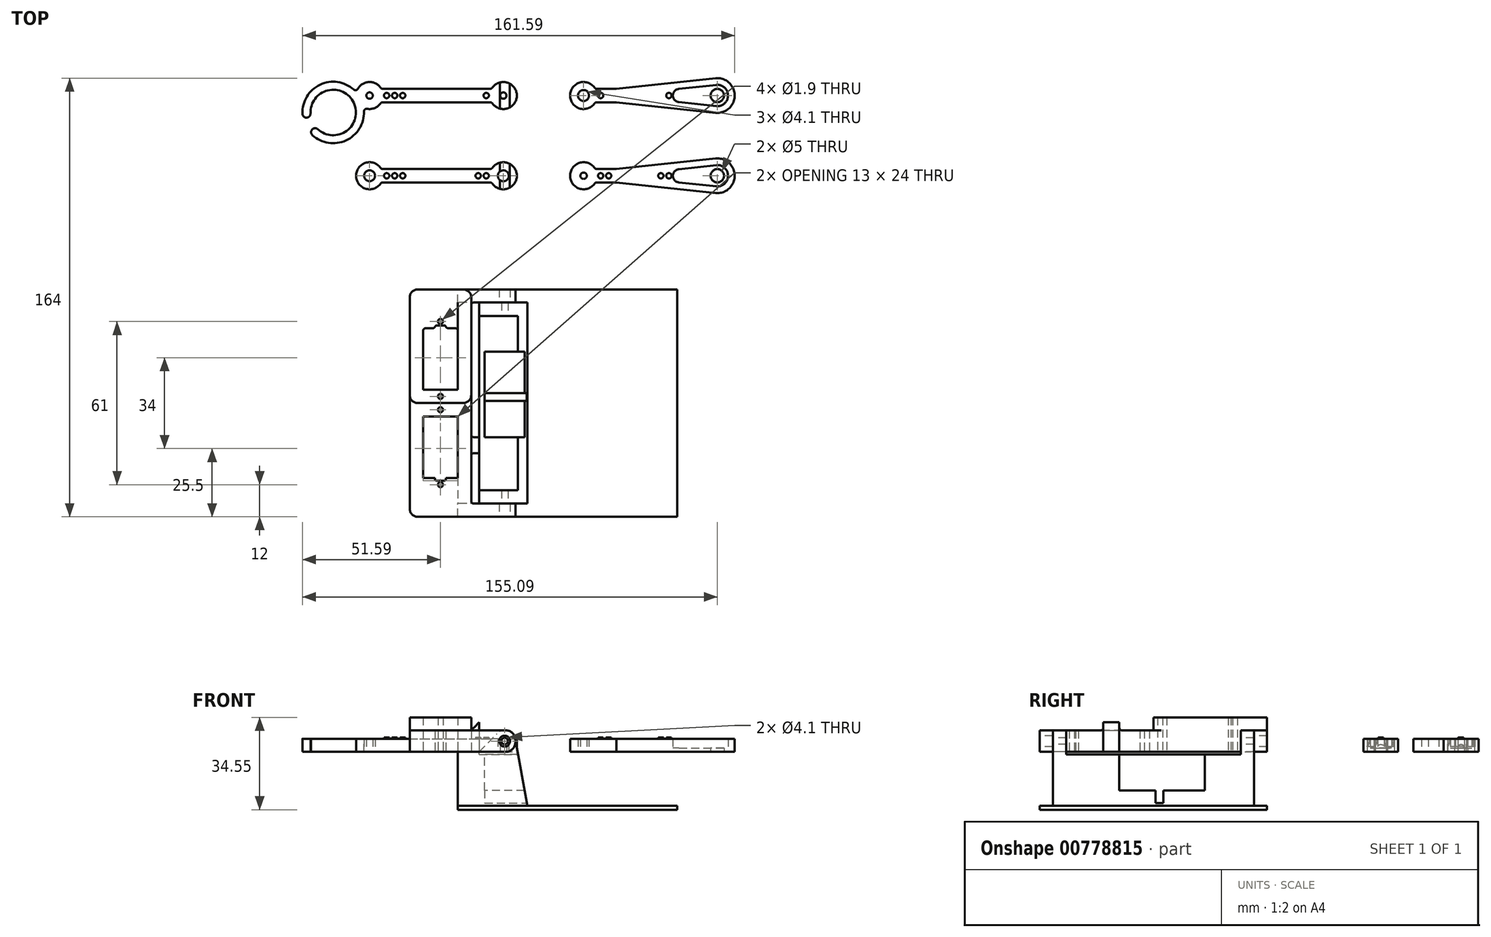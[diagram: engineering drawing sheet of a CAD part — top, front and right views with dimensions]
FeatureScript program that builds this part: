
annotation { "Feature Type Name" : "Feature", "Feature Type Description" : "" }
export const myFeature = defineFeature(function(context is Context, id is Id, definition is map)
    precondition{}
    {
        {
            assignVariable(context, id + "F0", {"name" : "armThickness", "anyValue" : 4.9 * mm});
        }
        {
            assignVariable(context, id + "F1", {"name" : "servoMountThick", "anyValue" : 1.5 * mm});
        }
        {
            var Q0;
            Q0=qCreatedBy(makeId("Top.planeOp"),FACE);
            var sketch = newSketch(context, id + "F2", { "sketchPlane" : qUnion([Q0])});
            skLineSegment(sketch, "E0", {"start": v(-65, 85) * mm, "end": v(-15, 85) * mm, "construction": true});
            skArc(sketch, "E1", {"start": v(-60.61, 87.5) * mm, "mid": v(-70.05, 85) * mm, "end": v(-60.61, 82.5) * mm});
            skArc(sketch, "E2", {"start": v(-19.39, 82.5) * mm, "mid": v(-9.95, 85) * mm, "end": v(-19.39, 87.5) * mm});
            skCircle(sketch, "E3", {"center": v(-65, 85) * mm, "radius": 2.05 * mm});
            skCircle(sketch, "E4", {"center": v(-15, 85) * mm, "radius": 2.05 * mm});
            skLineSegment(sketch, "E5", {"start": v(-60.61, 87.5) * mm, "end": v(-19.39, 87.5) * mm});
            skLineSegment(sketch, "E6", {"start": v(-60.61, 82.5) * mm, "end": v(-19.39, 82.5) * mm});
            skLineSegment(sketch, "E7", {"start": v(-40, 85) * mm, "end": v(-40, 87.5) * mm, "construction": true});
            skLineSegment(sketch, "E8", {"start": v(-40, 85) * mm, "end": v(-40, 82.5) * mm, "construction": true});
            skLineSegment(sketch, "E9", {"start": v(-65, 115) * mm, "end": v(-15, 115) * mm, "construction": true});
            skCircle(sketch, "E10", {"center": v(-15, 115) * mm, "radius": 1.2 * mm});
            skCircle(sketch, "E11", {"center": v(-65, 115) * mm, "radius": 1.2 * mm});
            skArc(sketch, "E12", {"start": v(-60.61, 117.5) * mm, "mid": v(-65.7, 120) * mm, "end": v(-69.9, 116.2) * mm});
            skArc(sketch, "E13", {"start": v(-19.39, 112.5) * mm, "mid": v(-9.95, 115) * mm, "end": v(-19.39, 117.5) * mm});
            skLineSegment(sketch, "E14", {"start": v(-60.61, 117.5) * mm, "end": v(-19.39, 117.5) * mm});
            skLineSegment(sketch, "E15", {"start": v(-19.39, 112.5) * mm, "end": v(-60.61, 112.5) * mm});
            skLineSegment(sketch, "E16", {"start": v(-40, 115) * mm, "end": v(-40, 117.5) * mm, "construction": true});
            skLineSegment(sketch, "E17", {"start": v(-40, 115) * mm, "end": v(-40, 112.5) * mm, "construction": true});
            skArc(sketch, "E18", {"start": v(-69.9, 116.2) * mm, "mid": v(-82.85, 119.34) * mm, "end": v(-90.08, 108.16) * mm});
            skArc(sketch, "E19", {"start": v(-84.34, 102.4) * mm, "mid": v(-70.9, 112.25) * mm, "end": v(-87.09, 108.29) * mm});
            skLineSegment(sketch, "E20", {"start": v(-78.6, 108.66) * mm, "end": v(-65, 115) * mm, "construction": true});
            skLineSegment(sketch, "E21", {"start": v(-78.6, 108.66) * mm, "end": v(-86.36, 100.18) * mm, "construction": true});
            skLineSegment(sketch, "E22", {"start": v(-78.6, 108.66) * mm, "end": v(-90.08, 108.16) * mm, "construction": true});
            skLineSegment(sketch, "E23", {"start": v(-90.08, 108.16) * mm, "end": v(-86.36, 100.18) * mm, "construction": true});
            skLineSegment(sketch, "E24", {"start": v(-88.22, 104.17) * mm, "end": v(-78.6, 108.66) * mm, "construction": true});
            skArc(sketch, "E25.trimOffspring", {"start": v(-67.24, 110.47) * mm, "mid": v(-63.52, 110.17) * mm, "end": v(-60.61, 112.5) * mm});
            skArc(sketch, "E26", {"start": v(-90.08, 108.16) * mm, "mid": v(-88.52, 106.73) * mm, "end": v(-87.09, 108.29) * mm});
            skArc(sketch, "E27", {"start": v(-84.34, 102.4) * mm, "mid": v(-86.46, 102.3) * mm, "end": v(-86.36, 100.18) * mm});
            skArc(sketch, "E28.trimOffspring", {"start": v(-86.36, 100.18) * mm, "mid": v(-73.15, 98.53) * mm, "end": v(-67.24, 110.47) * mm});
            skCircle(sketch, "E29", {"center": v(15, 115) * mm, "radius": 2.05 * mm});
            skArc(sketch, "E30", {"start": v(19.39, 117.5) * mm, "mid": v(9.95, 115) * mm, "end": v(19.39, 112.5) * mm});
            skArc(sketch, "E31", {"start": v(64.3, 108.54) * mm, "mid": v(71.5, 115) * mm, "end": v(64.3, 121.46) * mm});
            skLineSegment(sketch, "E32", {"start": v(65, 115) * mm, "end": v(15, 115) * mm, "construction": true});
            skLineSegment(sketch, "E33.bottom", {"start": v(15, 85) * mm, "end": v(-15, 85) * mm, "construction": true});
            skLineSegment(sketch, "E33.top", {"start": v(15, 115) * mm, "end": v(-15, 115) * mm, "construction": true});
            skLineSegment(sketch, "E33.left", {"start": v(15, 85) * mm, "end": v(15, 115) * mm, "construction": true});
            skLineSegment(sketch, "E33.right", {"start": v(-15, 85) * mm, "end": v(-15, 115) * mm, "construction": true});
            skPoint(sketch, "E33.middle", {"position": v(0, 100) * mm});
            skArc(sketch, "E34", {"start": v(64.63, 111.52) * mm, "mid": v(68.5, 115) * mm, "end": v(64.63, 118.48) * mm, "construction": true});
            skArc(sketch, "E35", {"start": v(50.69, 116.99) * mm, "mid": v(48.9, 115) * mm, "end": v(50.69, 113.01) * mm, "construction": true});
            skLineSegment(sketch, "E36", {"start": v(50.69, 116.99) * mm, "end": v(64.63, 118.48) * mm, "construction": true});
            skLineSegment(sketch, "E37", {"start": v(64.63, 111.52) * mm, "end": v(50.69, 113.01) * mm, "construction": true});
            skCircle(sketch, "E38", {"center": v(65, 115) * mm, "radius": 2.5 * mm});
            skLineSegment(sketch, "E39", {"start": v(-15, 100) * mm, "end": v(15, 100) * mm, "construction": true});
            skArc(sketch, "E40.MirrorCS", {"start": v(64.63, 88.48) * mm, "mid": v(68.5, 85) * mm, "end": v(64.63, 81.52) * mm, "construction": true});
            skArc(sketch, "E41.MirrorCS", {"start": v(50.69, 83.01) * mm, "mid": v(48.9, 85) * mm, "end": v(50.69, 86.99) * mm, "construction": true});
            skLineSegment(sketch, "E42.MirrorCS", {"start": v(50.69, 83.01) * mm, "end": v(64.63, 81.52) * mm, "construction": true});
            skCircle(sketch, "E43.MirrorC", {"center": v(65, 85) * mm, "radius": 2.5 * mm});
            skCircle(sketch, "E44.MirrorC", {"center": v(15, 85) * mm, "radius": 1.2 * mm});
            skLineSegment(sketch, "E45.MirrorCS", {"start": v(64.63, 88.48) * mm, "end": v(50.69, 86.99) * mm, "construction": true});
            skLineSegment(sketch, "E46.MirrorCS", {"start": v(65, 85) * mm, "end": v(15, 85) * mm, "construction": true});
            skArc(sketch, "E47.MirrorCS", {"start": v(19.39, 82.5) * mm, "mid": v(9.95, 85) * mm, "end": v(19.39, 87.5) * mm});
            skArc(sketch, "E48.MirrorCS", {"start": v(64.3, 91.46) * mm, "mid": v(71.5, 85) * mm, "end": v(64.3, 78.54) * mm});
            skLineSegment(sketch, "E49", {"start": v(64.3, 121.46) * mm, "end": v(27.27, 117.5) * mm});
            skLineSegment(sketch, "E50", {"start": v(27.27, 117.5) * mm, "end": v(19.39, 117.5) * mm});
            skLineSegment(sketch, "E51", {"start": v(19.39, 117.5) * mm, "end": v(19.39, 115) * mm, "construction": true});
            skLineSegment(sketch, "E52.MirrorCS", {"start": v(64.3, 108.54) * mm, "end": v(27.27, 112.5) * mm});
            skLineSegment(sketch, "E53.MirrorCS", {"start": v(27.27, 112.5) * mm, "end": v(19.39, 112.5) * mm});
            skLineSegment(sketch, "E54.MirrorCS", {"start": v(64.3, 91.46) * mm, "end": v(27.27, 87.5) * mm});
            skLineSegment(sketch, "E55.MirrorCS", {"start": v(27.27, 87.5) * mm, "end": v(19.39, 87.5) * mm});
            skLineSegment(sketch, "E56.MirrorCS", {"start": v(64.3, 78.54) * mm, "end": v(27.27, 82.5) * mm});
            skLineSegment(sketch, "E57.MirrorCS", {"start": v(27.27, 82.5) * mm, "end": v(19.39, 82.5) * mm});
            skCircle(sketch, "E58", {"center": v(-58.61, 115) * mm, "radius": 1 * mm, "construction": true});
            skCircle(sketch, "E59", {"center": v(-55.61, 115) * mm, "radius": 1 * mm, "construction": true});
            skCircle(sketch, "E60", {"center": v(-52.61, 115) * mm, "radius": 1 * mm, "construction": true});
            skCircle(sketch, "E61.MirrorC", {"center": v(-52.61, 85) * mm, "radius": 1 * mm, "construction": true});
            skCircle(sketch, "E62.MirrorC", {"center": v(-55.61, 85) * mm, "radius": 1 * mm, "construction": true});
            skCircle(sketch, "E63.MirrorC", {"center": v(-58.61, 85) * mm, "radius": 1 * mm, "construction": true});
            skCircle(sketch, "E64.MirrorC", {"center": v(-21.39, 115) * mm, "radius": 1 * mm, "construction": true});
            skCircle(sketch, "E65.MirrorC", {"center": v(-24.39, 85) * mm, "radius": 1 * mm, "construction": true});
            skCircle(sketch, "E66.MirrorC", {"center": v(-21.39, 85) * mm, "radius": 1 * mm, "construction": true});
            skLineSegment(sketch, "E67", {"start": v(0, 100) * mm, "end": v(0, 115) * mm, "construction": true});
            skCircle(sketch, "E68.MirrorC", {"center": v(21.39, 115) * mm, "radius": 1 * mm, "construction": true});
            skCircle(sketch, "E69.MirrorC", {"center": v(21.39, 85) * mm, "radius": 1 * mm, "construction": true});
            skCircle(sketch, "E70.MirrorC", {"center": v(24.39, 85) * mm, "radius": 1 * mm, "construction": true});
            skCircle(sketch, "E71", {"center": v(46.9, 115) * mm, "radius": 1 * mm, "construction": true});
            skCircle(sketch, "E72.MirrorC", {"center": v(46.9, 85) * mm, "radius": 1 * mm, "construction": true});
            skCircle(sketch, "E73", {"center": v(43.9, 85) * mm, "radius": 1 * mm, "construction": true});
            skSolve(sketch);
        }
        {
            var Q0;
            Q0 = qSketchRegion(id + "F2", true);
            extrude(context, id + "F3", {"entities" : qUnion([Q0]), "depth" : getVariable(context, 'armThickness'), "offsetDistance" : 25 * mm});
        }
        {
            var Q0;
            Q0=makeQuery(id+"F3.opExtrude","CAP_FACE",FACE,{"disambiguationData":[OSD([sQuery(id+"F2.wireOp",EDGE,"E29"),sQuery(id+"F2.wireOp",EDGE,"E30"),sQuery(id+"F2.wireOp",EDGE,"n4DpriQ1-nnHI-GnaH-HkeK-Vg4Ocvjjlzz4"),sQuery(id+"F2.wireOp",EDGE,"E31"),sQuery(id+"F2.wireOp",EDGE,"Jy9hjOYC-l6QO-X5wc-15VK-UPtCCQa5w7qG"),sQuery(id+"F2.wireOp",EDGE,"E7qWX5Tq-FMOK-UQwe-IjNl-v5n85ifmwsZO")])],"isStart":false});
            cPlane(context, id + "F4", {"entities" : qUnion([Q0]), "cplaneType" : CPlaneType.OFFSET, "offset" : 3.5 * mm, "oppositeDirection" : true, "width" : 150 * mm, "height" : 150 * mm});
        }
        {
            var Q0;
            Q0=qCreatedBy(id+"F4.planeOp",FACE);
            var sketch = newSketch(context, id + "F5", { "sketchPlane" : qUnion([Q0])});
            skLineSegment(sketch, "E74.0", {"start": v(50.69, 116.99) * mm, "end": v(64.63, 118.48) * mm, "construction": true});
            skArc(sketch, "E74.1", {"start": v(50.69, 116.99) * mm, "mid": v(48.9, 115) * mm, "end": v(50.69, 113.01) * mm, "construction": true});
            skLineSegment(sketch, "E74.2", {"start": v(64.63, 111.52) * mm, "end": v(50.69, 113.01) * mm, "construction": true});
            skArc(sketch, "E74.3", {"start": v(64.63, 111.52) * mm, "mid": v(68.5, 115) * mm, "end": v(64.63, 118.48) * mm, "construction": true});
            skLineSegment(sketch, "E75.0", {"start": v(50.63, 117.49) * mm, "end": v(64.57, 118.98) * mm});
            skArc(sketch, "E75.1", {"start": v(50.63, 117.49) * mm, "mid": v(48.4, 115) * mm, "end": v(50.63, 112.51) * mm});
            skLineSegment(sketch, "E75.2", {"start": v(64.57, 111.02) * mm, "end": v(50.63, 112.51) * mm});
            skArc(sketch, "E75.3", {"start": v(64.57, 111.02) * mm, "mid": v(69, 115) * mm, "end": v(64.57, 118.98) * mm});
            skArc(sketch, "E76.MirrorCS", {"start": v(64.57, 88.98) * mm, "mid": v(69, 85) * mm, "end": v(64.57, 81.02) * mm});
            skLineSegment(sketch, "E77.MirrorCS", {"start": v(50.63, 82.51) * mm, "end": v(64.57, 81.02) * mm});
            skLineSegment(sketch, "E78.MirrorCS", {"start": v(64.57, 88.98) * mm, "end": v(50.63, 87.49) * mm});
            skArc(sketch, "E79.MirrorCS", {"start": v(50.63, 82.51) * mm, "mid": v(48.4, 85) * mm, "end": v(50.63, 87.49) * mm});
            skSolve(sketch);
        }
        {
            var Q0;
            Q0 = qSketchRegion(id + "F5", true);
            var Q1;
            Q1=makeQuery(id+"F3.opExtrude","CAP_FACE",FACE,{"disambiguationData":[OSD([sQuery(id+"F2.wireOp",EDGE,"E29"),sQuery(id+"F2.wireOp",EDGE,"E30"),sQuery(id+"F2.wireOp",EDGE,"n4DpriQ1-nnHI-GnaH-HkeK-Vg4Ocvjjlzz4"),sQuery(id+"F2.wireOp",EDGE,"E31"),sQuery(id+"F2.wireOp",EDGE,"Jy9hjOYC-l6QO-X5wc-15VK-UPtCCQa5w7qG"),sQuery(id+"F2.wireOp",EDGE,"E7qWX5Tq-FMOK-UQwe-IjNl-v5n85ifmwsZO")])],"isStart":true});
            extrude(context, id + "F6", {"entities" : qUnion([Q0]), "operationType" : NewBodyOperationType.REMOVE, "endBound" : BoundingType.THROUGH_ALL, "depth" : getVariable(context, 'servoMountThick'), "endBoundEntityFace" : qUnion([Q1]), "offsetDistance" : 25 * mm});
        }
        {
            var Q0;
            Q0=qCreatedBy(makeId("Top.planeOp"),FACE);
            var sketch = newSketch(context, id + "F7", { "sketchPlane" : qUnion([Q0])});
            skLineSegment(sketch, "E80.bottom", {"start": v(-50, -42.5) * mm, "end": v(50, -42.5) * mm});
            skLineSegment(sketch, "E80.top", {"start": v(-50, 42.5) * mm, "end": v(50, 42.5) * mm});
            skLineSegment(sketch, "E80.left", {"start": v(-50, -42.5) * mm, "end": v(-50, 42.5) * mm});
            skLineSegment(sketch, "E80.right", {"start": v(50, -42.5) * mm, "end": v(50, 42.5) * mm});
            skPoint(sketch, "E80.middle", {"position": v(0, 0) * mm});
            skLineSegment(sketch, "E81", {"start": v(-6, 42.5) * mm, "end": v(-6, -42.5) * mm, "construction": true});
            skLineSegment(sketch, "E82", {"start": v(-14.5, 42.5) * mm, "end": v(-14.5, -42.5) * mm, "construction": true});
            skLineSegment(sketch, "E83.bottom", {"start": v(-8, -4.25) * mm, "end": v(-21, -4.25) * mm, "construction": true});
            skLineSegment(sketch, "E83.top", {"start": v(-8, 18.75) * mm, "end": v(-21, 18.75) * mm, "construction": true});
            skLineSegment(sketch, "E83.left", {"start": v(-8, -4.25) * mm, "end": v(-8, 18.75) * mm, "construction": true});
            skLineSegment(sketch, "E83.right", {"start": v(-21, -4.25) * mm, "end": v(-21, 18.75) * mm, "construction": true});
            skPoint(sketch, "E83.middle", {"position": v(-14.5, 7.25) * mm});
            skLineSegment(sketch, "E84", {"start": v(-27, -12.75) * mm, "end": v(-27, 37.6) * mm, "construction": true});
            skLineSegment(sketch, "E85", {"start": v(-27, 37.6) * mm, "end": v(-10.5, 37.6) * mm, "construction": true});
            skLineSegment(sketch, "E86", {"start": v(-10.5, 37.6) * mm, "end": v(-10.5, 42.5) * mm, "construction": true});
            skLineSegment(sketch, "E87", {"start": v(-10.5, -12.75) * mm, "end": v(-10.5, -18.75) * mm, "construction": true});
            skLineSegment(sketch, "E88", {"start": v(-10.5, -18.75) * mm, "end": v(-27, -18.75) * mm, "construction": true});
            skLineSegment(sketch, "E89", {"start": v(-27, -18.75) * mm, "end": v(-27, -37.6) * mm, "construction": true});
            skLineSegment(sketch, "E90", {"start": v(-27, -37.6) * mm, "end": v(-10.5, -37.6) * mm, "construction": true});
            skLineSegment(sketch, "E91", {"start": v(-10.5, -37.6) * mm, "end": v(-10.5, -42.5) * mm, "construction": true});
            skLineSegment(sketch, "E92.bottom", {"start": v(-10.5, 29.4) * mm, "end": v(-18.5, 29.4) * mm, "construction": true});
            skLineSegment(sketch, "E92.top", {"start": v(-10.5, 37.4) * mm, "end": v(-18.5, 37.4) * mm, "construction": true});
            skLineSegment(sketch, "E92.left", {"start": v(-10.5, 29.4) * mm, "end": v(-10.5, 37.4) * mm, "construction": true});
            skLineSegment(sketch, "E92.right", {"start": v(-18.5, 29.4) * mm, "end": v(-18.5, 37.4) * mm, "construction": true});
            skPoint(sketch, "E92.middle", {"position": v(-14.5, 33.4) * mm});
            skLineSegment(sketch, "E93.bottom", {"start": v(-10.5, -37.4) * mm, "end": v(-18.5, -37.4) * mm, "construction": true});
            skLineSegment(sketch, "E93.top", {"start": v(-10.5, -29.4) * mm, "end": v(-18.5, -29.4) * mm, "construction": true});
            skLineSegment(sketch, "E93.left", {"start": v(-10.5, -37.4) * mm, "end": v(-10.5, -29.4) * mm, "construction": true});
            skLineSegment(sketch, "E93.right", {"start": v(-18.5, -37.4) * mm, "end": v(-18.5, -29.4) * mm, "construction": true});
            skPoint(sketch, "E93.middle", {"position": v(-14.5, -33.4) * mm});
            skLineSegment(sketch, "E94.bottom", {"start": v(-32, 5) * mm, "end": v(-45, 5) * mm, "construction": true});
            skLineSegment(sketch, "E94.top", {"start": v(-32, 28) * mm, "end": v(-45, 28) * mm, "construction": true});
            skLineSegment(sketch, "E94.left", {"start": v(-32, 5) * mm, "end": v(-32, 28) * mm, "construction": true});
            skLineSegment(sketch, "E94.right", {"start": v(-45, 5) * mm, "end": v(-45, 28) * mm, "construction": true});
            skPoint(sketch, "E94.middle", {"position": v(-38.5, 16.5) * mm});
            skLineSegment(sketch, "E95.bottom", {"start": v(-32, -28) * mm, "end": v(-45, -28) * mm, "construction": true});
            skLineSegment(sketch, "E95.top", {"start": v(-32, -5) * mm, "end": v(-45, -5) * mm, "construction": true});
            skLineSegment(sketch, "E95.left", {"start": v(-32, -28) * mm, "end": v(-32, -5) * mm, "construction": true});
            skLineSegment(sketch, "E95.right", {"start": v(-45, -28) * mm, "end": v(-45, -5) * mm, "construction": true});
            skPoint(sketch, "E95.middle", {"position": v(-38.5, -16.5) * mm});
            skLineSegment(sketch, "E96", {"start": v(-38.5, 42.5) * mm, "end": v(-38.5, 28) * mm, "construction": true});
            skPoint(sketch, "E96.startSnap0", {"position": v(-38.5, 28) * mm});
            skLineSegment(sketch, "E97", {"start": v(-38.5, 28) * mm, "end": v(-38.5, 10.6) * mm, "construction": true});
            skLineSegment(sketch, "E98", {"start": v(-38.5, 10.6) * mm, "end": v(-38.5, -10.6) * mm, "construction": true});
            skLineSegment(sketch, "E99", {"start": v(-38.5, -10.6) * mm, "end": v(-38.5, -28) * mm, "construction": true});
            skLineSegment(sketch, "E100", {"start": v(-38.5, -28) * mm, "end": v(-38.5, -42.5) * mm, "construction": true});
            skCircle(sketch, "E101", {"center": v(-38.5, 10.6) * mm, "radius": 2.5 * mm, "construction": true});
            skCircle(sketch, "E102", {"center": v(-38.5, -10.6) * mm, "radius": 2.5 * mm, "construction": true});
            skLineSegment(sketch, "E103", {"start": v(-18.5, -29.4) * mm, "end": v(-18.5, -18.75) * mm, "construction": true});
            skLineSegment(sketch, "E104", {"start": v(-18.5, 29.4) * mm, "end": v(-18.5, 18.75) * mm, "construction": true});
            skLineSegment(sketch, "E105", {"start": v(-18, -4.25) * mm, "end": v(-18, -12.75) * mm, "construction": true});
            skLineSegment(sketch, "E106", {"start": v(-18, -12.75) * mm, "end": v(-14.5, -12.75) * mm, "construction": true});
            skLineSegment(sketch, "E107", {"start": v(-14.5, -12.75) * mm, "end": v(-11, -12.75) * mm, "construction": true});
            skLineSegment(sketch, "E108", {"start": v(-11, -12.75) * mm, "end": v(-11, -4.25) * mm, "construction": true});
            skLineSegment(sketch, "E109", {"start": v(-10.5, -12.75) * mm, "end": v(-27, -12.75) * mm, "construction": true});
            skCircle(sketch, "E110", {"center": v(-38.5, 30.5) * mm, "radius": 0.95 * mm, "construction": true});
            skCircle(sketch, "E111", {"center": v(-38.5, 2.5) * mm, "radius": 0.95 * mm, "construction": true});
            skLineSegment(sketch, "E112", {"start": v(-21, 0.75) * mm, "end": v(-8, 0.75) * mm, "construction": true});
            skLineSegment(sketch, "E113", {"start": v(-21, 3.25) * mm, "end": v(-8, 3.25) * mm, "construction": true});
            skSolve(sketch);
        }
        {
            var Q0;
            Q0=qCreatedBy(makeId("Top.planeOp"),FACE);
            var sketch = newSketch(context, id + "F8", { "sketchPlane" : qUnion([Q0])});
            skLineSegment(sketch, "E114.0", {"start": v(-10.5, 37.6) * mm, "end": v(-10.5, 42.5) * mm});
            skLineSegment(sketch, "E114.1", {"start": v(-27, 37.6) * mm, "end": v(-10.5, 37.6) * mm});
            skLineSegment(sketch, "E114.2", {"start": v(-27, -12.75) * mm, "end": v(-27, 37.6) * mm});
            skLineSegment(sketch, "E114.3", {"start": v(-50, -39.5) * mm, "end": v(-50, 39.5) * mm});
            skLineSegment(sketch, "E114.4", {"start": v(-10.5, -37.6) * mm, "end": v(-10.5, -42.5) * mm});
            skLineSegment(sketch, "E114.5", {"start": v(-27, -37.6) * mm, "end": v(-10.5, -37.6) * mm});
            skLineSegment(sketch, "E114.6", {"start": v(-27, -18.75) * mm, "end": v(-27, -37.6) * mm});
            skLineSegment(sketch, "E114.7", {"start": v(-10.5, -18.75) * mm, "end": v(-27, -18.75) * mm});
            skLineSegment(sketch, "E114.8", {"start": v(-10.5, -12.75) * mm, "end": v(-10.5, -18.75) * mm});
            skLineSegment(sketch, "E115", {"start": v(-10.5, -42.5) * mm, "end": v(-47, -42.5) * mm});
            skLineSegment(sketch, "E116", {"start": v(-47, 42.5) * mm, "end": v(-10.5, 42.5) * mm});
            skLineSegment(sketch, "E117.0", {"start": v(-32, 28) * mm, "end": v(-36.5, 28) * mm});
            skLineSegment(sketch, "E117.1", {"start": v(-45, 5) * mm, "end": v(-45, 28) * mm});
            skLineSegment(sketch, "E117.2", {"start": v(-32, 5) * mm, "end": v(-32, 28) * mm});
            skLineSegment(sketch, "E117.3", {"start": v(-32, 5) * mm, "end": v(-45, 5) * mm});
            skLineSegment(sketch, "E117.4", {"start": v(-32, -5) * mm, "end": v(-45, -5) * mm});
            skLineSegment(sketch, "E117.5", {"start": v(-32, -28) * mm, "end": v(-32, -5) * mm});
            skLineSegment(sketch, "E117.7", {"start": v(-45, -28) * mm, "end": v(-45, -5) * mm});
            skLineSegment(sketch, "E118.trimOffspring", {"start": v(-40.5, 28) * mm, "end": v(-45, 28) * mm});
            skPoint(sketch, "E119.visualSharp", {"position": v(-50, 42.5) * mm});
            skArc(sketch, "E119.filletArc", {"start": v(-47, 42.5) * mm, "mid": v(-49.12, 41.62) * mm, "end": v(-50, 39.5) * mm});
            skPoint(sketch, "E120.visualSharp", {"position": v(-50, -42.5) * mm});
            skArc(sketch, "E120.filletArc", {"start": v(-50, -39.5) * mm, "mid": v(-49.12, -41.62) * mm, "end": v(-47, -42.5) * mm});
            skLineSegment(sketch, "E121.0", {"start": v(-10.5, -12.75) * mm, "end": v(-27, -12.75) * mm});
            skLineSegment(sketch, "E122", {"start": v(-40.5, 28) * mm, "end": v(-40.5, 28.5) * mm});
            skLineSegment(sketch, "E123", {"start": v(-40, 29) * mm, "end": v(-37, 29) * mm});
            skLineSegment(sketch, "E124", {"start": v(-36.5, 28.5) * mm, "end": v(-36.5, 28) * mm});
            skPoint(sketch, "E125", {"position": v(-38.5, 29) * mm});
            skPoint(sketch, "E126.visualSharp", {"position": v(-40.5, 29) * mm});
            skArc(sketch, "E126.filletArc", {"start": v(-40, 29) * mm, "mid": v(-40.35, 28.85) * mm, "end": v(-40.5, 28.5) * mm});
            skPoint(sketch, "E127.visualSharp", {"position": v(-36.5, 29) * mm});
            skArc(sketch, "E127.filletArc", {"start": v(-36.5, 28.5) * mm, "mid": v(-36.65, 28.85) * mm, "end": v(-37, 29) * mm});
            skLineSegment(sketch, "E128.MirrorCS", {"start": v(-32, -28) * mm, "end": v(-36.5, -28) * mm});
            skLineSegment(sketch, "E129.MirrorCS", {"start": v(-36.5, -28.5) * mm, "end": v(-36.5, -28) * mm});
            skArc(sketch, "E130.MirrorCS", {"start": v(-36.5, -28.5) * mm, "mid": v(-36.65, -28.85) * mm, "end": v(-37, -29) * mm});
            skLineSegment(sketch, "E131.MirrorCS", {"start": v(-40, -29) * mm, "end": v(-37, -29) * mm});
            skArc(sketch, "E132.MirrorCS", {"start": v(-40, -29) * mm, "mid": v(-40.35, -28.85) * mm, "end": v(-40.5, -28.5) * mm});
            skLineSegment(sketch, "E133.MirrorCS", {"start": v(-40.5, -28) * mm, "end": v(-45, -28) * mm});
            skLineSegment(sketch, "E134.MirrorCS", {"start": v(-40.5, -28) * mm, "end": v(-40.5, -28.5) * mm});
            skCircle(sketch, "E135.0", {"center": v(-38.5, 30.5) * mm, "radius": 0.95 * mm});
            skCircle(sketch, "E135.1", {"center": v(-38.5, 2.5) * mm, "radius": 0.95 * mm});
            skCircle(sketch, "E136.MirrorC", {"center": v(-38.5, -30.5) * mm, "radius": 0.95 * mm});
            skCircle(sketch, "E137.MirrorC", {"center": v(-38.5, -2.5) * mm, "radius": 0.95 * mm});
            skSolve(sketch);
        }
        {
            var Q0;
            Q0 = qSketchRegion(id + "F8", true);
            extrude(context, id + "F9", {"entities" : qUnion([Q0]), "depth" : 8 * mm, "offsetDistance" : 25 * mm});
        }
        {
            var Q0;
            Q0=makeQuery(id+"F9.opExtrude","CAP_FACE",FACE,{"disambiguationData":[OSD([sQuery(id+"F8.wireOp",EDGE,"E114.0"),sQuery(id+"F8.wireOp",EDGE,"E114.1"),sQuery(id+"F8.wireOp",EDGE,"E114.2"),sQuery(id+"F8.wireOp",EDGE,"E114.3"),sQuery(id+"F8.wireOp",EDGE,"E114.4"),sQuery(id+"F8.wireOp",EDGE,"E114.5"),sQuery(id+"F8.wireOp",EDGE,"E114.6"),sQuery(id+"F8.wireOp",EDGE,"E114.7"),sQuery(id+"F8.wireOp",EDGE,"E114.8"),sQuery(id+"F8.wireOp",EDGE,"E115"),sQuery(id+"F8.wireOp",EDGE,"E116"),sQuery(id+"F8.wireOp",EDGE,"E117.0"),sQuery(id+"F8.wireOp",EDGE,"E117.1"),sQuery(id+"F8.wireOp",EDGE,"E117.2"),sQuery(id+"F8.wireOp",EDGE,"E117.3"),sQuery(id+"F8.wireOp",EDGE,"E117.4"),sQuery(id+"F8.wireOp",EDGE,"E117.5"),sQuery(id+"F8.wireOp",EDGE,"E117.6"),sQuery(id+"F8.wireOp",EDGE,"E117.7"),sQuery(id+"F8.wireOp",EDGE,"MD47gtlq-elkM-Q4DR-ia1A-ttEKbxPFzH0q"),sQuery(id+"F8.wireOp",EDGE,"fI236aIF-ESEJ-3lvR-EpUP-szV6qxp9SrXm"),sQuery(id+"F8.wireOp",EDGE,"E118.trimOffspring"),sQuery(id+"F8.wireOp",EDGE,"9ecd033c-57ae-48f4-bd77-c65d463de197.trimOffspring"),sQuery(id+"F8.wireOp",EDGE,"E119.filletArc"),sQuery(id+"F8.wireOp",EDGE,"E120.filletArc"),sQuery(id+"F8.wireOp",EDGE,"E121.0")])],"isStart":false});
            var sketch = newSketch(context, id + "F10", { "sketchPlane" : qUnion([Q0])});
            skLineSegment(sketch, "E138", {"start": v(-32, 5) * mm, "end": v(-32, 5) * mm});
            skLineSegment(sketch, "E139.0", {"start": v(-32, 28) * mm, "end": v(-32, 28) * mm});
            skLineSegment(sketch, "E139.1", {"start": v(-32, 5) * mm, "end": v(-32, 28) * mm});
            skLineSegment(sketch, "E139.4", {"start": v(-45, 5) * mm, "end": v(-45, 28) * mm});
            skLineSegment(sketch, "E139.5", {"start": v(-32, 5) * mm, "end": v(-45, 5) * mm});
            skLineSegment(sketch, "E140.0", {"start": v(-40.5, 28) * mm, "end": v(-45, 28) * mm});
            skLineSegment(sketch, "E140.1", {"start": v(-40.5, 28) * mm, "end": v(-40.5, 28.5) * mm});
            skArc(sketch, "E140.2", {"start": v(-40, 29) * mm, "mid": v(-40.35, 28.85) * mm, "end": v(-40.5, 28.5) * mm});
            skLineSegment(sketch, "E140.3", {"start": v(-40, 29) * mm, "end": v(-37, 29) * mm});
            skCircle(sketch, "E140.4", {"center": v(-38.5, 30.5) * mm, "radius": 0.95 * mm});
            skArc(sketch, "E140.5", {"start": v(-36.5, 28.5) * mm, "mid": v(-36.65, 28.85) * mm, "end": v(-37, 29) * mm});
            skLineSegment(sketch, "E140.6", {"start": v(-36.5, 28.5) * mm, "end": v(-36.5, 28) * mm});
            skLineSegment(sketch, "E140.7", {"start": v(-32, 28) * mm, "end": v(-36.5, 28) * mm});
            skCircle(sketch, "E141.0", {"center": v(-38.5, 2.5) * mm, "radius": 0.95 * mm});
            skArc(sketch, "E142.0", {"start": v(-47, 42.5) * mm, "mid": v(-49.12, 41.62) * mm, "end": v(-50, 39.5) * mm});
            skLineSegment(sketch, "E143", {"start": v(-50, 39.5) * mm, "end": v(-50, 3) * mm});
            skLineSegment(sketch, "E144", {"start": v(-38.5, 2.5) * mm, "end": v(-38.5, -2.5) * mm, "construction": true});
            skPoint(sketch, "E145", {"position": v(-38.5, 0) * mm});
            skLineSegment(sketch, "E146", {"start": v(-47, 0) * mm, "end": v(-30, 0) * mm});
            skLineSegment(sketch, "E147", {"start": v(-27, 3) * mm, "end": v(-27, 39.5) * mm});
            skLineSegment(sketch, "E148", {"start": v(-47, 42.5) * mm, "end": v(-30, 42.5) * mm});
            skArc(sketch, "E149", {"start": v(-50, 3) * mm, "mid": v(-49.12, 0.88) * mm, "end": v(-47, 0) * mm});
            skArc(sketch, "E150", {"start": v(-30, 0) * mm, "mid": v(-27.88, 0.88) * mm, "end": v(-27, 3) * mm});
            skArc(sketch, "E151", {"start": v(-27, 39.5) * mm, "mid": v(-27.88, 41.62) * mm, "end": v(-30, 42.5) * mm});
            skSolve(sketch);
        }
        {
            var Q0;
            Q0 = qSketchRegion(id + "F10", true);
            extrude(context, id + "F11", {"entities" : qUnion([Q0]), "operationType" : NewBodyOperationType.ADD, "depth" : getVariable(context, 'armThickness'), "offsetDistance" : 25 * mm});
        }
        {
            var Q0;
            Q0=makeQuery(id+"F9.opExtrude","SWEPT_FACE",FACE,{"disambiguationData":[OSD([sQuery(id+"F8.wireOp",EDGE,"E115")])]});
            var sketch = newSketch(context, id + "F12", { "sketchPlane" : qUnion([Q0])});
            skLineSegment(sketch, "E152", {"start": v(-14.5, 0) * mm, "end": v(-14.5, 8) * mm, "construction": true});
            skCircle(sketch, "E153", {"center": v(-14.5, 4) * mm, "radius": 2.05 * mm});
            skSolve(sketch);
        }
        {
            var Q0;
            Q0 = qSketchRegion(id + "F12", true);
            extrude(context, id + "F13", {"entities" : qUnion([Q0]), "operationType" : NewBodyOperationType.REMOVE, "endBound" : BoundingType.THROUGH_ALL, "oppositeDirection" : true, "depth" : 25 * mm, "offsetDistance" : 25 * mm});
        }
        {
            var Q0;
            Q0=makeQuery(id+"F9.opExtrude","SWEPT_FACE",FACE,{"disambiguationData":[OSD([sQuery(id+"F8.wireOp",EDGE,"E114.7")])]});
            var sketch = newSketch(context, id + "F14", { "sketchPlane" : qUnion([Q0])});
            skLineSegment(sketch, "E154", {"start": v(-10.5, 8) * mm, "end": v(-10.5, 20) * mm});
            skLineSegment(sketch, "E155", {"start": v(-10.5, 20) * mm, "end": v(-15.5, 20) * mm});
            skLineSegment(sketch, "E156", {"start": v(-15.5, 20) * mm, "end": v(-27, 8) * mm});
            skLineSegment(sketch, "E157", {"start": v(-27, 8) * mm, "end": v(-10.5, 8) * mm});
            skSolve(sketch);
        }
        {
            var Q0;
            Q0 = qSketchRegion(id + "F14", true);
            var Q1;
            Q1=makeQuery(id+"F9.opExtrude","SWEPT_FACE",FACE,{"disambiguationData":[OSD([sQuery(id+"F8.wireOp",EDGE,"E121.0")])]});
            extrude(context, id + "F15", {"entities" : qUnion([Q0]), "operationType" : NewBodyOperationType.ADD, "endBound" : BoundingType.UP_TO_SURFACE, "oppositeDirection" : true, "depth" : 25 * mm, "endBoundEntityFace" : qUnion([Q1]), "offsetDistance" : 25 * mm});
        }
        {
            var Q0;
            Q0=makeQuery(id+"F9.opExtrude","CAP_EDGE",EDGE,{"disambiguationData":[OSD([sQuery(id+"F8.wireOp",EDGE,"E114.4")])],"isStart":false});
            var Q1;
            Q1=makeQuery(id+"F9.opExtrude","CAP_EDGE",EDGE,{"disambiguationData":[OSD([sQuery(id+"F8.wireOp",EDGE,"E114.4")])],"isStart":true});
            var Q2;
            Q2=makeQuery(id+"F9.opExtrude","CAP_EDGE",EDGE,{"disambiguationData":[OSD([sQuery(id+"F8.wireOp",EDGE,"E114.0")])],"isStart":true});
            var Q3;
            Q3=makeQuery(id+"F9.opExtrude","CAP_EDGE",EDGE,{"disambiguationData":[OSD([sQuery(id+"F8.wireOp",EDGE,"E114.0")])],"isStart":false});
            var Q4;
            Q4=makeQuery(id+"F9.opExtrude","CAP_EDGE",EDGE,{"disambiguationData":[OSD([sQuery(id+"F8.wireOp",EDGE,"E114.8")])],"isStart":true});
            var Q5;
            Q5=makeQuery(id+"F15.opExtrude","SWEPT_EDGE",EDGE,{"disambiguationData":[OSD([sQuery(id+"F14.wireOp",EDGE,"E155"),sQuery(id+"F14.wireOp",EDGE,"E156")])]});
            var Q6;
            Q6=makeQuery(id+"F15.opExtrude","SWEPT_EDGE",EDGE,{"disambiguationData":[OSD([sQuery(id+"F14.wireOp",EDGE,"E154"),sQuery(id+"F14.wireOp",EDGE,"E155")])]});
            var Q7;
            Q7=makeQuery(id+"F15.opExtrude","SWEPT_EDGE",EDGE,{"disambiguationData":[OSD([sQuery(id+"F8.wireOp",EDGE,"E114.6"),sQuery(id+"F8.wireOp",EDGE,"E114.7"),sQuery(id+"F14.wireOp",EDGE,"E156"),sQuery(id+"F14.wireOp",EDGE,"E157")])]});
            fillet(context, id + "F16", {"entities" : qUnion([Q0, Q1, Q2, Q3, Q4, Q5, Q6, Q7]), "radius" : 3.5 * mm, "tangentPropagation" : true, "allowEdgeOverflow" : false});
        }
        {
            var Q0;
            Q0=makeQuery(id+"F9.opExtrude","SWEPT_EDGE",EDGE,{"disambiguationData":[OSD([sQuery(id+"F8.wireOp",EDGE,"MD47gtlq-elkM-Q4DR-ia1A-ttEKbxPFzH0q"),sQuery(id+"F8.wireOp",EDGE,"E118.trimOffspring")])]});
            var Q1;
            Q1=makeQuery(id+"F9.opExtrude","SWEPT_EDGE",EDGE,{"disambiguationData":[OSD([sQuery(id+"F8.wireOp",EDGE,"E117.0"),sQuery(id+"F8.wireOp",EDGE,"MD47gtlq-elkM-Q4DR-ia1A-ttEKbxPFzH0q")])]});
            var Q2;
            Q2=makeQuery(id+"F9.opExtrude","SWEPT_EDGE",EDGE,{"disambiguationData":[OSD([sQuery(id+"F8.wireOp",EDGE,"fI236aIF-ESEJ-3lvR-EpUP-szV6qxp9SrXm"),sQuery(id+"F8.wireOp",EDGE,"9ecd033c-57ae-48f4-bd77-c65d463de197.trimOffspring")])]});
            var Q3;
            Q3=makeQuery(id+"F9.opExtrude","SWEPT_EDGE",EDGE,{"disambiguationData":[OSD([sQuery(id+"F8.wireOp",EDGE,"E117.6"),sQuery(id+"F8.wireOp",EDGE,"fI236aIF-ESEJ-3lvR-EpUP-szV6qxp9SrXm")])]});
            var Q4;
            Q4=makeQuery(id+"F15.opExtrude","SWEPT_EDGE",EDGE,{"disambiguationData":[OSD([sQuery(id+"F8.wireOp",EDGE,"E114.6"),sQuery(id+"F8.wireOp",EDGE,"E114.7"),sQuery(id+"F14.wireOp",EDGE,"E156"),sQuery(id+"F14.wireOp",EDGE,"E157")])]});
            var Q5;
            Q5=makeQuery(id+"F9.opExtrude","SWEPT_EDGE",EDGE,{"disambiguationData":[OSD([sQuery(id+"F8.wireOp",EDGE,"E114.2"),sQuery(id+"F8.wireOp",EDGE,"E114.9")])]});
            var Q6;
            Q6=makeQuery(id+"F9.opExtrude","SWEPT_EDGE",EDGE,{"disambiguationData":[OSD([sQuery(id+"F8.wireOp",EDGE,"E114.6"),sQuery(id+"F8.wireOp",EDGE,"E114.7")])]});
            var Q7;
            Q7=makeQuery(id+"F9.opExtrude","SWEPT_EDGE",EDGE,{"disambiguationData":[OSD([sQuery(id+"F8.wireOp",EDGE,"E114.1"),sQuery(id+"F8.wireOp",EDGE,"E114.2")])]});
            var Q8;
            Q8=makeQuery(id+"F9.opExtrude","SWEPT_EDGE",EDGE,{"disambiguationData":[OSD([sQuery(id+"F8.wireOp",EDGE,"E114.5"),sQuery(id+"F8.wireOp",EDGE,"E114.6")])]});
            var Q9;
            {var subQ0=sQuery(id+"F8.wireOp",EDGE,"E114.9");Q9=makeQuery(id+"F16.opFillet","TWEAK_EDGE",EDGE,{"derivedFrom":[makeQuery(id+"F15.boolean.opBoolean","MERGE",VERTEX,{"derivedFrom":[makeQuery(id+"F9.opExtrude","CAP_VERTEX",VERTEX,{"disambiguationData":[OSD([sQuery(id+"F8.wireOp",EDGE,"E114.2"),subQ0])],"isStart":false}),makeQuery(id+"F15.opExtrude","CAP_VERTEX",VERTEX,{"disambiguationData":[OSD([sQuery(id+"F8.wireOp",EDGE,"E114.6"),sQuery(id+"F8.wireOp",EDGE,"E114.7"),subQ0,sQuery(id+"F14.wireOp",EDGE,"E156"),sQuery(id+"F14.wireOp",EDGE,"E157")])],"isStart":false})]})]});}
            var Q10;
            {var subQ0=sQuery(id+"F8.wireOp",EDGE,"E114.7");var subQ1=sQuery(id+"F8.wireOp",EDGE,"E114.6");Q10=makeQuery(id+"F16.opFillet","TWEAK_EDGE",EDGE,{"derivedFrom":[makeQuery(id+"F15.boolean.opBoolean","MERGE",VERTEX,{"derivedFrom":[makeQuery(id+"F9.opExtrude","CAP_VERTEX",VERTEX,{"disambiguationData":[OSD([subQ1,subQ0])],"isStart":false}),makeQuery(id+"F15.opExtrude","CAP_VERTEX",VERTEX,{"disambiguationData":[OSD([subQ1,subQ0,sQuery(id+"F14.wireOp",EDGE,"E156"),sQuery(id+"F14.wireOp",EDGE,"E157")])],"isStart":true})]})]});}
            var Q11;
            Q11=makeQuery(id+"F3.opExtrude","SWEPT_EDGE",EDGE,{"disambiguationData":[OSD([sQuery(id+"F2.wireOp",EDGE,"E30"),sQuery(id+"F2.wireOp",EDGE,"E50")])]});
            var Q12;
            Q12=makeQuery(id+"F3.opExtrude","SWEPT_EDGE",EDGE,{"disambiguationData":[OSD([sQuery(id+"F2.wireOp",EDGE,"E47.MirrorCS"),sQuery(id+"F2.wireOp",EDGE,"E55.MirrorCS")])]});
            var Q13;
            Q13=makeQuery(id+"F3.opExtrude","SWEPT_EDGE",EDGE,{"disambiguationData":[OSD([sQuery(id+"F2.wireOp",EDGE,"E12"),sQuery(id+"F2.wireOp",EDGE,"E14")])]});
            var Q14;
            Q14=makeQuery(id+"F3.opExtrude","SWEPT_EDGE",EDGE,{"disambiguationData":[OSD([sQuery(id+"F2.wireOp",EDGE,"E13"),sQuery(id+"F2.wireOp",EDGE,"E14")])]});
            var Q15;
            Q15=makeQuery(id+"F3.opExtrude","SWEPT_EDGE",EDGE,{"disambiguationData":[OSD([sQuery(id+"F2.wireOp",EDGE,"E2"),sQuery(id+"F2.wireOp",EDGE,"E5")])]});
            var Q16;
            Q16=makeQuery(id+"F3.opExtrude","SWEPT_EDGE",EDGE,{"disambiguationData":[OSD([sQuery(id+"F2.wireOp",EDGE,"E1"),sQuery(id+"F2.wireOp",EDGE,"E5")])]});
            var Q17;
            Q17=makeQuery(id+"F3.opExtrude","SWEPT_EDGE",EDGE,{"disambiguationData":[OSD([sQuery(id+"F2.wireOp",EDGE,"E47.MirrorCS"),sQuery(id+"F2.wireOp",EDGE,"E57.MirrorCS")])]});
            var Q18;
            Q18=makeQuery(id+"F3.opExtrude","SWEPT_EDGE",EDGE,{"disambiguationData":[OSD([sQuery(id+"F2.wireOp",EDGE,"E30"),sQuery(id+"F2.wireOp",EDGE,"E53.MirrorCS")])]});
            var Q19;
            Q19=makeQuery(id+"F3.opExtrude","SWEPT_EDGE",EDGE,{"disambiguationData":[OSD([sQuery(id+"F2.wireOp",EDGE,"E13"),sQuery(id+"F2.wireOp",EDGE,"E15")])]});
            var Q20;
            Q20=makeQuery(id+"F3.opExtrude","SWEPT_EDGE",EDGE,{"disambiguationData":[OSD([sQuery(id+"F2.wireOp",EDGE,"E2"),sQuery(id+"F2.wireOp",EDGE,"E6")])]});
            var Q21;
            Q21=makeQuery(id+"F3.opExtrude","SWEPT_EDGE",EDGE,{"disambiguationData":[OSD([sQuery(id+"F2.wireOp",EDGE,"E1"),sQuery(id+"F2.wireOp",EDGE,"E6")])]});
            var Q22;
            Q22=makeQuery(id+"F3.opExtrude","SWEPT_EDGE",EDGE,{"disambiguationData":[OSD([sQuery(id+"F2.wireOp",EDGE,"E15"),sQuery(id+"F2.wireOp",EDGE,"E25.trimOffspring")])]});
            var Q23;
            Q23=makeQuery(id+"F3.opExtrude","SWEPT_EDGE",EDGE,{"disambiguationData":[OSD([sQuery(id+"F2.wireOp",EDGE,"E25.trimOffspring"),sQuery(id+"F2.wireOp",EDGE,"E28.trimOffspring")])]});
            var Q24;
            Q24=makeQuery(id+"F3.opExtrude","SWEPT_EDGE",EDGE,{"disambiguationData":[OSD([sQuery(id+"F2.wireOp",EDGE,"E12"),sQuery(id+"F2.wireOp",EDGE,"E18")])]});
            fillet(context, id + "F17", {"entities" : qUnion([Q0, Q1, Q2, Q3, Q4, Q5, Q6, Q7, Q8, Q9, Q10, Q11, Q12, Q13, Q14, Q15, Q16, Q17, Q18, Q19, Q20, Q21, Q22, Q23, Q24]), "radius" : 1 * mm, "tangentPropagation" : true, "allowEdgeOverflow" : false});
        }
        {
            var Q0;
            Q0=makeQuery(id+"F9.opExtrude","SWEPT_FACE",FACE,{"disambiguationData":[OSD([sQuery(id+"F8.wireOp",EDGE,"E115")])]});
            var sketch = newSketch(context, id + "F18", { "sketchPlane" : qUnion([Q0])});
            skLineSegment(sketch, "E158.bottom", {"start": v(-8, -13.4) * mm, "end": v(-21, -13.4) * mm, "construction": true});
            skLineSegment(sketch, "E158.top", {"start": v(-8, 9.6) * mm, "end": v(-21, 9.6) * mm, "construction": true});
            skLineSegment(sketch, "E158.left", {"start": v(-8, -13.4) * mm, "end": v(-8, 9.6) * mm, "construction": true});
            skLineSegment(sketch, "E158.right", {"start": v(-21, -13.4) * mm, "end": v(-21, 9.6) * mm, "construction": true});
            skPoint(sketch, "E158.middle", {"position": v(-14.5, -1.9) * mm});
            skCircle(sketch, "E159", {"center": v(-14.5, 4) * mm, "radius": 2.5 * mm, "construction": true});
            skLineSegment(sketch, "E160", {"start": v(-21, -13.4) * mm, "end": v(-21, -18.15) * mm, "construction": true});
            skLineSegment(sketch, "E161", {"start": v(-21, -18.15) * mm, "end": v(-8, -18.15) * mm, "construction": true});
            skLineSegment(sketch, "E162", {"start": v(-8, -18.15) * mm, "end": v(-8, -13.4) * mm, "construction": true});
            skSolve(sketch);
        }
        {
            var Q0;
            Q0=makeQuery(id+"F9.opExtrude","SWEPT_FACE",FACE,{"disambiguationData":[OSD([sQuery(id+"F8.wireOp",EDGE,"E114.5")])]});
            var sketch = newSketch(context, id + "F19", { "sketchPlane" : qUnion([Q0])});
            skArc(sketch, "E163", {"start": v(17.36, 6.8) * mm, "mid": v(16.05, 7.69) * mm, "end": v(14.5, 8) * mm});
            skLineSegment(sketch, "E164", {"start": v(14.5, 8) * mm, "end": v(14.5, -20.15) * mm, "construction": true});
            skLineSegment(sketch, "E165", {"start": v(14.5, -20.15) * mm, "end": v(32, -20.15) * mm});
            skArc(sketch, "E166", {"start": v(14.5, 8) * mm, "mid": v(11.94, 7.07) * mm, "end": v(10.57, 4.72) * mm});
            skLineSegment(sketch, "E167", {"start": v(10.57, 4.72) * mm, "end": v(6, -20.15) * mm});
            skLineSegment(sketch, "E168", {"start": v(6, -20.15) * mm, "end": v(14.5, -20.15) * mm});
            skLineSegment(sketch, "E169", {"start": v(17.36, 6.8) * mm, "end": v(24, 0) * mm});
            skLineSegment(sketch, "E170", {"start": v(24, 0) * mm, "end": v(32, 0) * mm});
            skLineSegment(sketch, "E171", {"start": v(32, 0) * mm, "end": v(32, -20.15) * mm});
            skCircle(sketch, "E172", {"center": v(14.5, 4) * mm, "radius": 1.2 * mm});
            skSolve(sketch);
        }
        {
            var Q0;
            Q0 = qSketchRegion(id + "F19", true);
            var Q1;
            Q1=makeQuery(id+"F9.opExtrude","SWEPT_FACE",FACE,{"disambiguationData":[OSD([sQuery(id+"F8.wireOp",EDGE,"E114.1")])]});
            extrude(context, id + "F20", {"entities" : qUnion([Q0]), "endBound" : BoundingType.UP_TO_SURFACE, "depth" : getVariable(context, 'armThickness'), "endBoundEntityFace" : qUnion([Q1]), "offsetDistance" : 25 * mm});
        }
        {
            var Q0;
            Q0=makeQuery(id+"F20.opExtrude","SWEPT_FACE",FACE,{"disambiguationData":[OSD([sQuery(id+"F19.wireOp",EDGE,"E165"),sQuery(id+"F19.wireOp",EDGE,"E168")])]});
            var sketch = newSketch(context, id + "F21", { "sketchPlane" : qUnion([Q0])});
            skLineSegment(sketch, "E173.bottom", {"start": v(-32, 42.5) * mm, "end": v(50, 42.5) * mm});
            skLineSegment(sketch, "E173.top", {"start": v(-32, -42.5) * mm, "end": v(50, -42.5) * mm});
            skLineSegment(sketch, "E173.left", {"start": v(-32, 42.5) * mm, "end": v(-32, -42.5) * mm});
            skLineSegment(sketch, "E173.right", {"start": v(50, 42.5) * mm, "end": v(50, -42.5) * mm});
            skSolve(sketch);
        }
        {
            var Q0;
            Q0 = qSketchRegion(id + "F21", true);
            extrude(context, id + "F22", {"entities" : qUnion([Q0]), "operationType" : NewBodyOperationType.ADD, "depth" : 1.5 * mm, "offsetDistance" : 25 * mm});
        }
        {
            var Q0;
            Q0=makeQuery(id+"F20.opExtrude","SWEPT_FACE",FACE,{"disambiguationData":[OSD([sQuery(id+"F19.wireOp",EDGE,"E170")])]});
            var sketch = newSketch(context, id + "F23", { "sketchPlane" : qUnion([Q0])});
            skLineSegment(sketch, "E174.bottom", {"start": v(-24, -32.6) * mm, "end": v(-6, -32.6) * mm});
            skLineSegment(sketch, "E174.top", {"start": v(-24, 32.6) * mm, "end": v(-6, 32.6) * mm});
            skLineSegment(sketch, "E174.left", {"start": v(-24, -32.6) * mm, "end": v(-24, 32.6) * mm});
            skLineSegment(sketch, "E174.right", {"start": v(-6, -32.6) * mm, "end": v(-6, 32.6) * mm});
            skSolve(sketch);
        }
        {
            var Q0;
            Q0 = qSketchRegion(id + "F23", true);
            extrude(context, id + "F24", {"entities" : qUnion([Q0]), "operationType" : NewBodyOperationType.REMOVE, "oppositeDirection" : true, "depth" : 1 * mm, "offsetDistance" : 25 * mm, "hasSecondDirection" : true, "secondDirectionBound" : SecondDirectionBoundingType.THROUGH_ALL, "secondDirectionOppositeDirection" : false, "secondDirectionDepth" : 25 * mm});
        }
        {
            var Q0;
            {var subQ0=sQuery(id+"F8.wireOp",EDGE,"E121.0");Q0=makeQuery(id+"F15.boolean.opBoolean","MERGE",FACE,{"derivedFrom":[makeQuery(id+"F9.opExtrude","SWEPT_FACE",FACE,{"disambiguationData":[OSD([subQ0])]}),makeQuery(id+"F15.opExtrude","CAP_FACE",FACE,{"disambiguationData":[OSD([subQ0])],"isStart":false})]});}
            var sketch = newSketch(context, id + "F25", { "sketchPlane" : qUnion([Q0])});
            skLineSegment(sketch, "E175.0", {"start": v(8, 9.6) * mm, "end": v(21, 9.6) * mm, "construction": true});
            skLineSegment(sketch, "E175.1", {"start": v(21, -13.4) * mm, "end": v(21, 9.6) * mm, "construction": true});
            skLineSegment(sketch, "E175.2", {"start": v(8, -13.4) * mm, "end": v(8, 9.6) * mm, "construction": true});
            skLineSegment(sketch, "E175.3", {"start": v(8, -13.4) * mm, "end": v(21, -13.4) * mm, "construction": true});
            skLineSegment(sketch, "E176.0", {"start": v(7, -14.4) * mm, "end": v(7, 10.6) * mm});
            skLineSegment(sketch, "E176.1", {"start": v(7, -14.4) * mm, "end": v(22, -14.4) * mm});
            skLineSegment(sketch, "E176.2", {"start": v(22, -14.4) * mm, "end": v(22, 10.6) * mm});
            skLineSegment(sketch, "E176.3", {"start": v(7, 10.6) * mm, "end": v(22, 10.6) * mm});
            skSolve(sketch);
        }
        {
            var Q0;
            Q0 = qSketchRegion(id + "F25", true);
            extrude(context, id + "F26", {"entities" : qUnion([Q0]), "operationType" : NewBodyOperationType.REMOVE, "depth" : 32 * mm, "offsetDistance" : 25 * mm});
        }
        {
            var Q0;
            Q0=makeQuery(id+"F26.boolean.opBoolean","COPY",FACE,{"derivedFrom":makeQuery(id+"F26.opExtrude","CAP_FACE",FACE,{"disambiguationData":[OSD([sQuery(id+"F25.wireOp",EDGE,"E176.0"),sQuery(id+"F25.wireOp",EDGE,"E176.1"),sQuery(id+"F25.wireOp",EDGE,"E176.2"),sQuery(id+"F25.wireOp",EDGE,"E176.3")])],"isStart":true})});
            var Q1;
            Q1=sQuery(id+"F7.wireOp",VERTEX,"E112.end");
            cPlane(context, id + "F27", {"entities" : qUnion([Q0, Q1]), "cplaneType" : CPlaneType.PLANE_POINT, "offset" : 25 * mm, "width" : 150 * mm, "height" : 150 * mm});
        }
        {
            var Q0;
            Q0=qCreatedBy(id+"F27.planeOp",FACE);
            var sketch = newSketch(context, id + "F28", { "sketchPlane" : qUnion([Q0])});
            skLineSegment(sketch, "E177.0", {"start": v(8, -13.4) * mm, "end": v(21, -13.4) * mm, "construction": true});
            skLineSegment(sketch, "E177.1", {"start": v(21, -13.4) * mm, "end": v(21, -18.15) * mm, "construction": true});
            skLineSegment(sketch, "E177.2", {"start": v(21, -18.15) * mm, "end": v(8, -18.15) * mm, "construction": true});
            skLineSegment(sketch, "E177.3", {"start": v(8, -18.15) * mm, "end": v(8, -13.4) * mm, "construction": true});
            skLineSegment(sketch, "E178.0", {"start": v(7, -19.15) * mm, "end": v(7, -12.4) * mm, "construction": true});
            skLineSegment(sketch, "E178.1", {"start": v(22, -19.15) * mm, "end": v(7, -19.15) * mm});
            skLineSegment(sketch, "E178.2", {"start": v(22, -12.4) * mm, "end": v(22, -19.15) * mm});
            skLineSegment(sketch, "E178.3", {"start": v(7, -12.4) * mm, "end": v(22, -12.4) * mm});
            skLineSegment(sketch, "E179", {"start": v(7, -12.4) * mm, "end": v(4, -12.4) * mm});
            skLineSegment(sketch, "E180", {"start": v(4, -12.4) * mm, "end": v(4, -19.15) * mm});
            skLineSegment(sketch, "E181", {"start": v(4, -19.15) * mm, "end": v(7, -19.15) * mm});
            skSolve(sketch);
        }
        {
            var Q0;
            Q0 = qSketchRegion(id + "F28", true);
            extrude(context, id + "F29", {"entities" : qUnion([Q0]), "operationType" : NewBodyOperationType.REMOVE, "depth" : 3 * mm, "offsetDistance" : 25 * mm});
        }
        {
            var Q0;
            Q0=makeQuery(id+"F3.opExtrude","CAP_FACE",FACE,{"disambiguationData":[OSD([sQuery(id+"F2.wireOp",EDGE,"E29"),sQuery(id+"F2.wireOp",EDGE,"E30"),sQuery(id+"F2.wireOp",EDGE,"E31"),sQuery(id+"F2.wireOp",EDGE,"E38"),sQuery(id+"F2.wireOp",EDGE,"E49"),sQuery(id+"F2.wireOp",EDGE,"E50"),sQuery(id+"F2.wireOp",EDGE,"E52.MirrorCS"),sQuery(id+"F2.wireOp",EDGE,"E53.MirrorCS")])],"isStart":false});
            var sketch = newSketch(context, id + "F30", { "sketchPlane" : qUnion([Q0])});
            skCircle(sketch, "E182.0", {"center": v(-58.61, 115) * mm, "radius": 1 * mm});
            skCircle(sketch, "E182.1", {"center": v(-55.61, 115) * mm, "radius": 1 * mm});
            skCircle(sketch, "E182.2", {"center": v(-52.61, 115) * mm, "radius": 1 * mm});
            skCircle(sketch, "E182.3", {"center": v(-21.39, 115) * mm, "radius": 1 * mm});
            skCircle(sketch, "E182.4", {"center": v(21.39, 115) * mm, "radius": 1 * mm});
            skCircle(sketch, "E182.5", {"center": v(46.9, 115) * mm, "radius": 1 * mm});
            skCircle(sketch, "E182.6", {"center": v(46.9, 85) * mm, "radius": 1 * mm});
            skCircle(sketch, "E182.7", {"center": v(43.9, 85) * mm, "radius": 1 * mm});
            skCircle(sketch, "E182.8", {"center": v(24.39, 85) * mm, "radius": 1 * mm});
            skCircle(sketch, "E182.9", {"center": v(21.39, 85) * mm, "radius": 1 * mm});
            skCircle(sketch, "E182.10", {"center": v(-21.39, 85) * mm, "radius": 1 * mm});
            skCircle(sketch, "E182.11", {"center": v(-24.39, 85) * mm, "radius": 1 * mm});
            skCircle(sketch, "E182.12", {"center": v(-52.61, 85) * mm, "radius": 1 * mm});
            skCircle(sketch, "E182.13", {"center": v(-55.61, 85) * mm, "radius": 1 * mm});
            skCircle(sketch, "E182.14", {"center": v(-58.61, 85) * mm, "radius": 1 * mm});
            skSolve(sketch);
        }
        {
            var Q0;
            Q0 = qSketchRegion(id + "F30", true);
            var Q1;
            Q1 = qConstructionFilter(qBodyType(qCreatedBy(id + "F30" ,EDGE), BodyType.WIRE), ConstructionObject.NO);
            extrude(context, id + "F31", {"entities" : qUnion([Q0]), "operationType" : NewBodyOperationType.ADD, "surfaceOperationType" : NewSurfaceOperationType.ADD, "surfaceEntities" : qUnion([Q1]), "depth" : 0.5 * mm, "offsetDistance" : 25 * mm});
        }
    });
